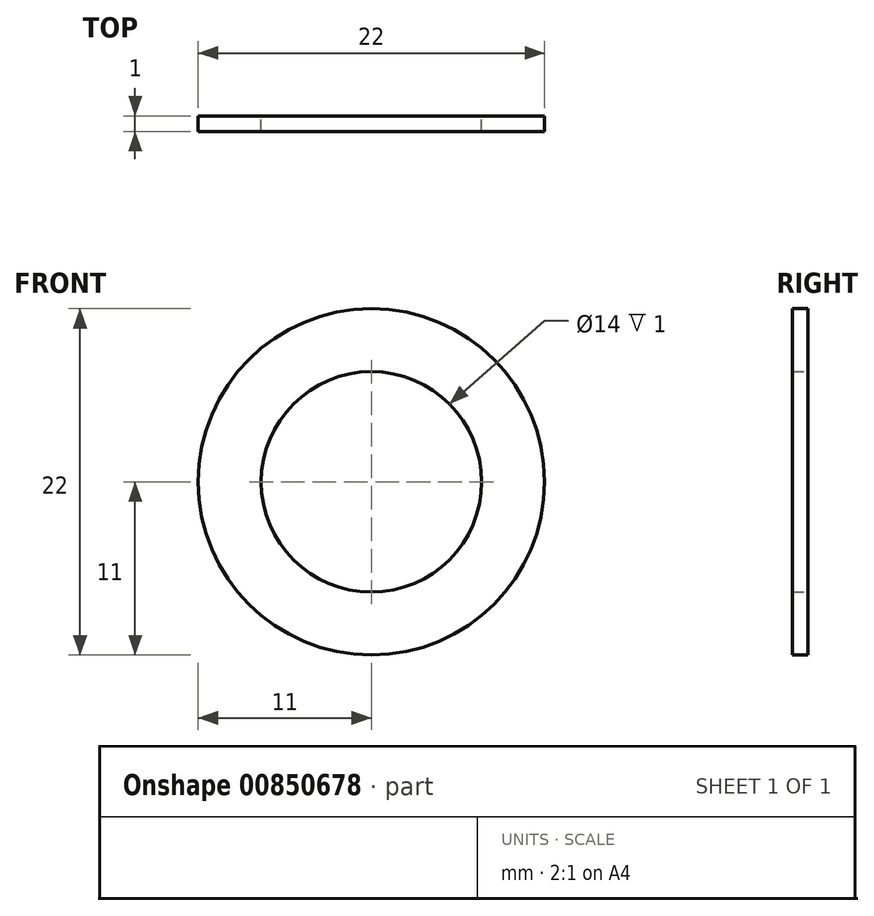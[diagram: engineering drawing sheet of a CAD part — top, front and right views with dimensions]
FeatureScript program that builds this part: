
annotation { "Feature Type Name" : "Feature", "Feature Type Description" : "" }
export const myFeature = defineFeature(function(context is Context, id is Id, definition is map)
    precondition{}
    {
        {
            var Q0;
            Q0=qCreatedBy(makeId("Front.planeOp"),FACE);
            var sketch = newSketch(context, id + "F0", { "sketchPlane" : qUnion([Q0])});
            skCircle(sketch, "E0", {"center": v(0, 0) * mm, "radius": 11 * mm});
            skCircle(sketch, "E1", {"center": v(0, 0) * mm, "radius": 7 * mm});
            skSolve(sketch);
        }
        {
            var Q0;
            Q0 = qSketchRegion(id + "F0", true);
            extrude(context, id + "F1", {"entities" : qUnion([Q0]), "depth" : 1 * mm, "offsetDistance" : 25 * mm});
        }
    });
